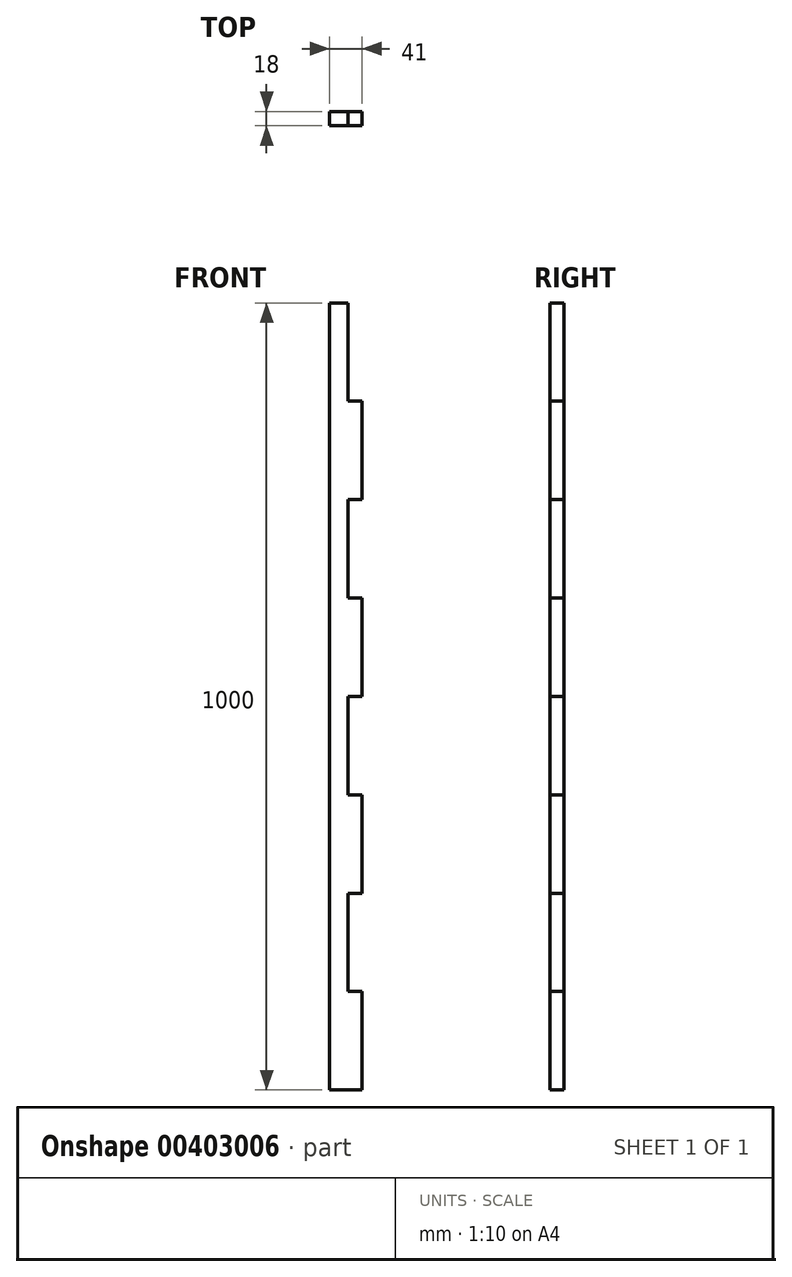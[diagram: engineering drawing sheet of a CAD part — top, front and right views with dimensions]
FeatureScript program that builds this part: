
annotation { "Feature Type Name" : "Feature", "Feature Type Description" : "" }
export const myFeature = defineFeature(function(context is Context, id is Id, definition is map)
    precondition{}
    {
        {
            var Q0;
            Q0=qCreatedBy(makeId("Front.planeOp"),FACE);
            var sketch = newSketch(context, id + "F0", { "sketchPlane" : qUnion([Q0])});
            skLineSegment(sketch, "E0.bottom", {"start": v(0, 0) * mm, "end": v(41, 0) * mm});
            skLineSegment(sketch, "E0.top", {"start": v(0, 1000) * mm, "end": v(23, 1000) * mm});
            skLineSegment(sketch, "E0.left", {"start": v(0, 0) * mm, "end": v(0, 1000) * mm});
            skLineSegment(sketch, "E0.right", {"start": v(41, 0) * mm, "end": v(41, 125) * mm});
            skLineSegment(sketch, "E1.top", {"start": v(41, 875) * mm, "end": v(23, 875) * mm});
            skLineSegment(sketch, "E1.right", {"start": v(23, 1000) * mm, "end": v(23, 875) * mm});
            skLineSegment(sketch, "E2.bottom", {"start": v(41, 750) * mm, "end": v(23, 750) * mm});
            skLineSegment(sketch, "E2.top", {"start": v(41, 625) * mm, "end": v(23, 625) * mm});
            skLineSegment(sketch, "E2.right", {"start": v(23, 750) * mm, "end": v(23, 625) * mm});
            skLineSegment(sketch, "E3.bottom", {"start": v(41, 500) * mm, "end": v(23, 500) * mm});
            skLineSegment(sketch, "E3.top", {"start": v(41, 375) * mm, "end": v(23, 375) * mm});
            skLineSegment(sketch, "E3.right", {"start": v(23, 500) * mm, "end": v(23, 375) * mm});
            skLineSegment(sketch, "E4.bottom", {"start": v(41, 250) * mm, "end": v(23, 250) * mm});
            skLineSegment(sketch, "E4.top", {"start": v(41, 125) * mm, "end": v(23, 125) * mm});
            skLineSegment(sketch, "E4.right", {"start": v(23, 250) * mm, "end": v(23, 125) * mm});
            skLineSegment(sketch, "E5.trimOffspring", {"start": v(41, 750) * mm, "end": v(41, 875) * mm});
            skLineSegment(sketch, "E6.trimOffspring", {"start": v(41, 500) * mm, "end": v(41, 625) * mm});
            skLineSegment(sketch, "E7.trimOffspring", {"start": v(41, 250) * mm, "end": v(41, 375) * mm});
            skSolve(sketch);
        }
        {
            var Q0;
            Q0=makeQuery(id+"F0.imprint","IMPRINT",FACE,{"disambiguationData":[TD([[makeQuery(id+"F0.imprint","IMPRINT",EDGE,{"derivedFrom":sQuery(id+"F0.wireOp",EDGE,"kHmZVxOG-gPJc-REYJ-O9rl-HYASeAGw87Q2.bottom")}),1.0]])]});
            var Q1;
            Q1=makeQuery(id+"F0.imprint","IMPRINT",FACE,{"disambiguationData":[TD([[makeQuery(id+"F0.imprint","IMPRINT",EDGE,{"derivedFrom":sQuery(id+"F0.wireOp",EDGE,"E0.bottom")}),1.0]])]});
            extrude(context, id + "F1", {"entities" : qUnion([Q0, Q1]), "depth" : 18 * mm});
        }
    });
